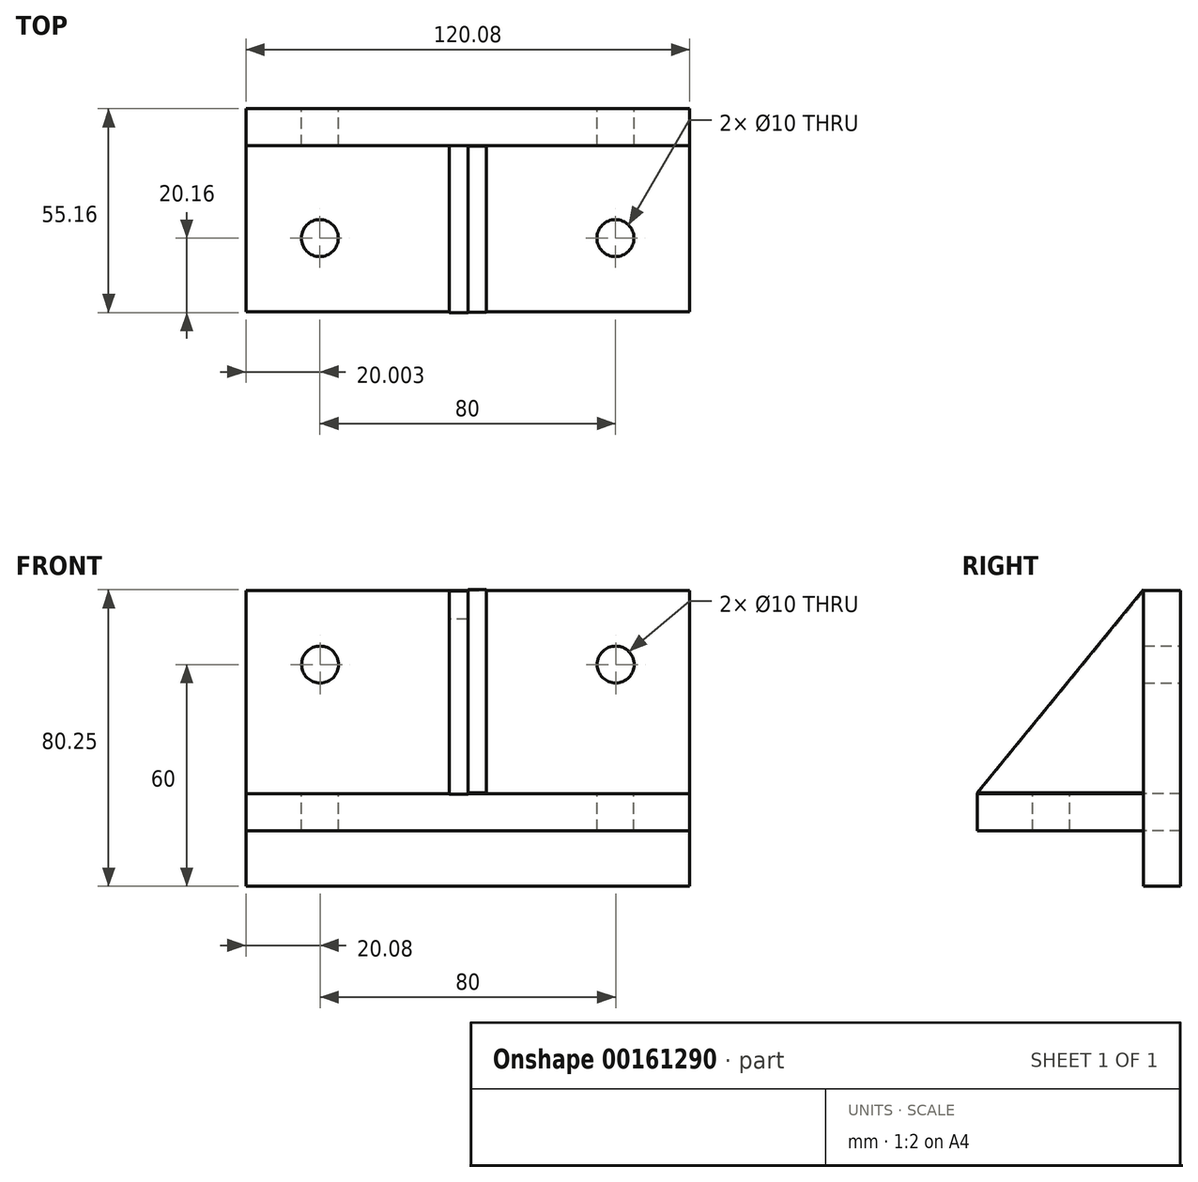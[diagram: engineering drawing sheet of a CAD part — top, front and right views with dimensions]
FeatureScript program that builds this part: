
annotation { "Feature Type Name" : "Feature", "Feature Type Description" : "" }
export const myFeature = defineFeature(function(context is Context, id is Id, definition is map)
    precondition{}
    {
        {
            var Q0;
            Q0=qCreatedBy(makeId("Front.planeOp"),FACE);
            var sketch = newSketch(context, id + "F0", { "sketchPlane" : qUnion([Q0])});
            skLineSegment(sketch, "E0.bottom", {"start": v(-60, 40) * mm, "end": v(60, 40) * mm});
            skLineSegment(sketch, "E0.top", {"start": v(-60, -40) * mm, "end": v(60, -40) * mm});
            skLineSegment(sketch, "E0.left", {"start": v(-60, 40) * mm, "end": v(-60, -40) * mm});
            skLineSegment(sketch, "E0.right", {"start": v(60, 40) * mm, "end": v(60, -40) * mm});
            skPoint(sketch, "E0.middle", {"position": v(0, 0) * mm});
            skCircle(sketch, "E1", {"center": v(-40, 20) * mm, "radius": 5 * mm});
            skCircle(sketch, "E2", {"center": v(40, 20) * mm, "radius": 5 * mm});
            skSolve(sketch);
        }
        {
            var Q0;
            Q0 = qSketchRegion(id + "F0", true);
            extrude(context, id + "F1", {"entities" : qUnion([Q0]), "depth" : 10 * mm});
        }
        {
            var Q0;
            Q0=qCreatedBy(makeId("Front.planeOp"),FACE);
            var sketch = newSketch(context, id + "F2", { "sketchPlane" : qUnion([Q0])});
            skLineSegment(sketch, "E3.bottom", {"start": v(-60.08, -24.97) * mm, "end": v(59.92, -24.97) * mm});
            skLineSegment(sketch, "E3.top", {"start": v(-60.08, -14.97) * mm, "end": v(59.92, -14.97) * mm});
            skLineSegment(sketch, "E3.left", {"start": v(-60.08, -24.97) * mm, "end": v(-60.08, -14.97) * mm});
            skLineSegment(sketch, "E3.right", {"start": v(59.92, -24.97) * mm, "end": v(59.92, -14.97) * mm});
            skSolve(sketch);
        }
        {
            var Q0;
            Q0 = qSketchRegion(id + "F2", true);
            extrude(context, id + "F3", {"entities" : qUnion([Q0]), "operationType" : NewBodyOperationType.ADD, "depth" : 55 * mm});
        }
        {
            var Q0;
            Q0=makeQuery(id+"F3.opExtrude","SWEPT_FACE",FACE,{"disambiguationData":[OSD([sQuery(id+"F2.wireOp",EDGE,"E3.top")])]});
            var sketch = newSketch(context, id + "F4", { "sketchPlane" : qUnion([Q0])});
            skCircle(sketch, "E4", {"center": v(-40.08, -35) * mm, "radius": 5 * mm});
            skCircle(sketch, "E5", {"center": v(39.92, -35) * mm, "radius": 5 * mm});
            skSolve(sketch);
        }
        {
            var Q0;
            Q0 = qSketchRegion(id + "F4", true);
            extrude(context, id + "F5", {"entities" : qUnion([Q0]), "operationType" : NewBodyOperationType.REMOVE, "oppositeDirection" : true, "depth" : 25 * mm});
        }
        {
            var Q0;
            Q0=qCreatedBy(makeId("Right.planeOp"),FACE);
            var sketch = newSketch(context, id + "F6", { "sketchPlane" : qUnion([Q0])});
            skLineSegment(sketch, "E6", {"start": v(-9.97, 39.96) * mm, "end": v(-55.16, -15.04) * mm});
            skLineSegment(sketch, "E7", {"start": v(-55.16, -15.04) * mm, "end": v(-10.16, -15.04) * mm});
            skLineSegment(sketch, "E8", {"start": v(-9.97, 39.96) * mm, "end": v(-10.16, -15.04) * mm});
            skSolve(sketch);
        }
        {
            var Q0;
            Q0 = qSketchRegion(id + "F6", true);
            extrude(context, id + "F7", {"entities" : qUnion([Q0]), "operationType" : NewBodyOperationType.ADD, "oppositeDirection" : true, "depth" : 5 * mm});
        }
        {
            var Q0;
            Q0=qCreatedBy(makeId("Right.planeOp"),FACE);
            var sketch = newSketch(context, id + "F8", { "sketchPlane" : qUnion([Q0])});
            skLineSegment(sketch, "E9", {"start": v(-10.06, 40.25) * mm, "end": v(-55.06, -14.75) * mm});
            skLineSegment(sketch, "E10", {"start": v(-55.06, -14.75) * mm, "end": v(-10.06, -14.75) * mm});
            skLineSegment(sketch, "E11", {"start": v(-10.06, -14.75) * mm, "end": v(-10.06, 40.25) * mm});
            skSolve(sketch);
        }
        {
            var Q0;
            Q0 = qSketchRegion(id + "F8", true);
            extrude(context, id + "F9", {"entities" : qUnion([Q0]), "operationType" : NewBodyOperationType.ADD, "depth" : 5 * mm});
        }
    });
